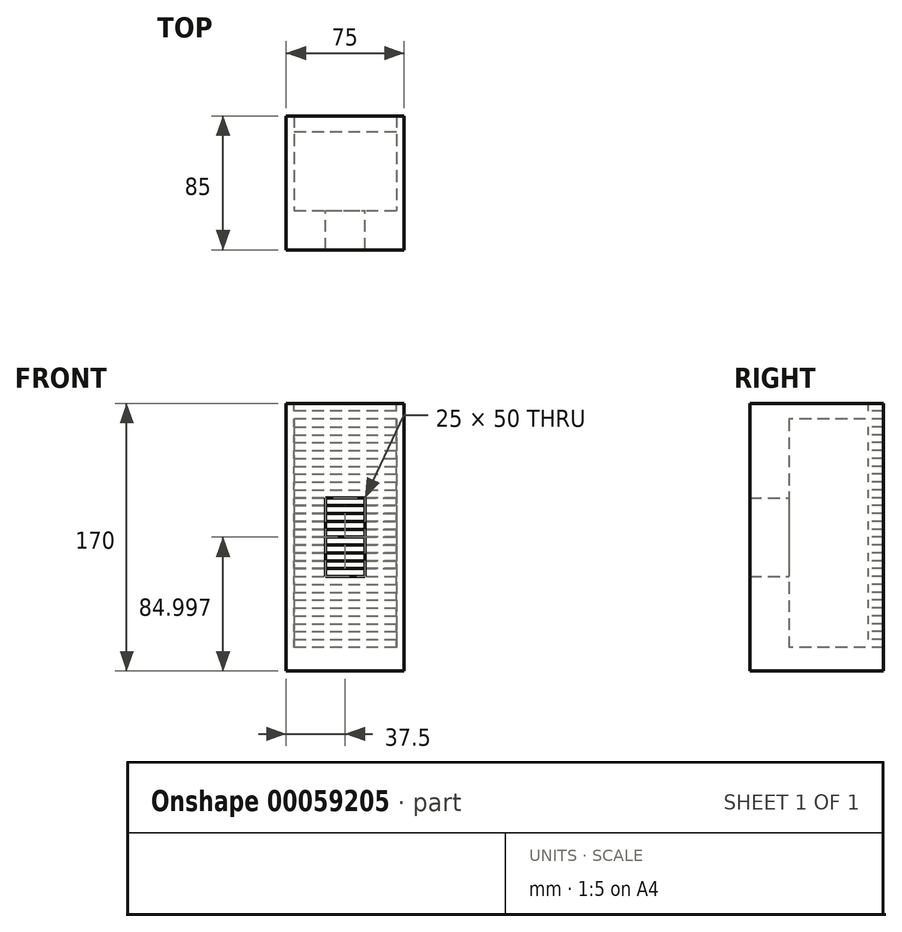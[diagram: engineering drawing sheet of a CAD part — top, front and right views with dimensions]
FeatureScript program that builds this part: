
annotation { "Feature Type Name" : "Feature", "Feature Type Description" : "" }
export const myFeature = defineFeature(function(context is Context, id is Id, definition is map)
    precondition{}
    {
        {
            var Q0;
            Q0=qCreatedBy(makeId("Right.planeOp"),FACE);
            var sketch = newSketch(context, id + "F0", { "sketchPlane" : qUnion([Q0])});
            skLineSegment(sketch, "E0", {"start": v(-41.76, 67.65) * mm, "end": v(-41.76, -102.35) * mm});
            skLineSegment(sketch, "E1", {"start": v(-41.76, -102.35) * mm, "end": v(-31.76, -102.35) * mm});
            skLineSegment(sketch, "E2", {"start": v(-31.76, -102.35) * mm, "end": v(-31.76, 67.65) * mm});
            skLineSegment(sketch, "E3", {"start": v(-31.76, 67.65) * mm, "end": v(-41.76, 67.65) * mm});
            skSolve(sketch);
        }
        {
            var Q0;
            Q0=qSketchRegion(id+"F0",true);
            extrude(context, id + "F1", {"entities" : qUnion([Q0]), "endBound" : BoundingType.SYMMETRIC, "depth" : 75 * mm});
        }
        {
            var Q0;
            Q0=makeQuery(id+"F1.opExtrude","SWEPT_FACE",FACE,{"disambiguationData":[OSD([sQuery(id+"F0.wireOp",EDGE,"E0")])]});
            var sketch = newSketch(context, id + "F2", { "sketchPlane" : qUnion([Q0])});
            skLineSegment(sketch, "E4.bottom", {"start": v(-32.5, 67.55) * mm, "end": v(32.5, 67.55) * mm});
            skLineSegment(sketch, "E4.top", {"start": v(-32.5, 62.65) * mm, "end": v(32.5, 62.65) * mm});
            skLineSegment(sketch, "E4.left", {"start": v(-32.5, 67.55) * mm, "end": v(-32.5, 62.65) * mm});
            skLineSegment(sketch, "E4.right", {"start": v(32.5, 67.55) * mm, "end": v(32.5, 62.65) * mm});
            skLineSegment(sketch, "E5.0.1.0", {"start": v(-32.5, 57.55) * mm, "end": v(32.5, 57.55) * mm});
            skLineSegment(sketch, "E5.0.1.1", {"start": v(-32.5, 57.55) * mm, "end": v(-32.5, 52.65) * mm});
            skLineSegment(sketch, "E5.0.1.2", {"start": v(-32.5, 52.65) * mm, "end": v(32.5, 52.65) * mm});
            skLineSegment(sketch, "E5.0.1.3", {"start": v(32.5, 57.55) * mm, "end": v(32.5, 52.65) * mm});
            skLineSegment(sketch, "E5.0.2.0", {"start": v(-32.5, 47.55) * mm, "end": v(32.5, 47.55) * mm});
            skLineSegment(sketch, "E5.0.2.1", {"start": v(-32.5, 47.55) * mm, "end": v(-32.5, 42.65) * mm});
            skLineSegment(sketch, "E5.0.2.2", {"start": v(-32.5, 42.65) * mm, "end": v(32.5, 42.65) * mm});
            skLineSegment(sketch, "E5.0.2.3", {"start": v(32.5, 47.55) * mm, "end": v(32.5, 42.65) * mm});
            skLineSegment(sketch, "E5.0.3.0", {"start": v(-32.5, 37.55) * mm, "end": v(32.5, 37.55) * mm});
            skLineSegment(sketch, "E5.0.3.1", {"start": v(-32.5, 37.55) * mm, "end": v(-32.5, 32.65) * mm});
            skLineSegment(sketch, "E5.0.3.2", {"start": v(-32.5, 32.65) * mm, "end": v(32.5, 32.65) * mm});
            skLineSegment(sketch, "E5.0.3.3", {"start": v(32.5, 37.55) * mm, "end": v(32.5, 32.65) * mm});
            skLineSegment(sketch, "E5.0.4.0", {"start": v(-32.5, 27.55) * mm, "end": v(32.5, 27.55) * mm});
            skLineSegment(sketch, "E5.0.4.1", {"start": v(-32.5, 27.55) * mm, "end": v(-32.5, 22.65) * mm});
            skLineSegment(sketch, "E5.0.4.2", {"start": v(-32.5, 22.65) * mm, "end": v(32.5, 22.65) * mm});
            skLineSegment(sketch, "E5.0.4.3", {"start": v(32.5, 27.55) * mm, "end": v(32.5, 22.65) * mm});
            skLineSegment(sketch, "E5.direction1", {"start": v(-32.5, 67.55) * mm, "end": v(-7.5, 67.55) * mm, "construction": true});
            skLineSegment(sketch, "E5.direction2", {"start": v(-32.5, 67.55) * mm, "end": v(-32.5, 57.55) * mm, "construction": true});
            skLineSegment(sketch, "E6.0.0.5", {"start": v(-32.5, 17.55) * mm, "end": v(32.5, 17.55) * mm});
            skLineSegment(sketch, "E6.3.0.5", {"start": v(-32.5, 17.55) * mm, "end": v(-32.5, 12.65) * mm});
            skLineSegment(sketch, "E6.6.0.5", {"start": v(-32.5, 12.65) * mm, "end": v(32.5, 12.65) * mm});
            skLineSegment(sketch, "E6.9.0.5", {"start": v(32.5, 17.55) * mm, "end": v(32.5, 12.65) * mm});
            skLineSegment(sketch, "E6.0.0.6", {"start": v(-32.5, 7.55) * mm, "end": v(32.5, 7.55) * mm});
            skLineSegment(sketch, "E6.3.0.6", {"start": v(-32.5, 7.55) * mm, "end": v(-32.5, 2.65) * mm});
            skLineSegment(sketch, "E6.6.0.6", {"start": v(-32.5, 2.65) * mm, "end": v(32.5, 2.65) * mm});
            skLineSegment(sketch, "E6.9.0.6", {"start": v(32.5, 7.55) * mm, "end": v(32.5, 2.65) * mm});
            skLineSegment(sketch, "E6.0.0.7", {"start": v(-32.5, -2.45) * mm, "end": v(32.5, -2.45) * mm});
            skLineSegment(sketch, "E6.3.0.7", {"start": v(-32.5, -2.45) * mm, "end": v(-32.5, -7.35) * mm});
            skLineSegment(sketch, "E6.6.0.7", {"start": v(-32.5, -7.35) * mm, "end": v(32.5, -7.35) * mm});
            skLineSegment(sketch, "E6.9.0.7", {"start": v(32.5, -2.45) * mm, "end": v(32.5, -7.35) * mm});
            skLineSegment(sketch, "E7.0.0.8", {"start": v(-32.5, -12.45) * mm, "end": v(32.5, -12.45) * mm});
            skLineSegment(sketch, "E7.3.0.8", {"start": v(-32.5, -12.45) * mm, "end": v(-32.5, -17.35) * mm});
            skLineSegment(sketch, "E7.6.0.8", {"start": v(-32.5, -17.35) * mm, "end": v(32.5, -17.35) * mm});
            skLineSegment(sketch, "E7.9.0.8", {"start": v(32.5, -12.45) * mm, "end": v(32.5, -17.35) * mm});
            skLineSegment(sketch, "E7.0.0.9", {"start": v(-32.5, -22.45) * mm, "end": v(32.5, -22.45) * mm});
            skLineSegment(sketch, "E7.3.0.9", {"start": v(-32.5, -22.45) * mm, "end": v(-32.5, -27.35) * mm});
            skLineSegment(sketch, "E7.6.0.9", {"start": v(-32.5, -27.35) * mm, "end": v(32.5, -27.35) * mm});
            skLineSegment(sketch, "E7.9.0.9", {"start": v(32.5, -22.45) * mm, "end": v(32.5, -27.35) * mm});
            skLineSegment(sketch, "E7.0.0.10", {"start": v(-32.5, -32.45) * mm, "end": v(32.5, -32.45) * mm});
            skLineSegment(sketch, "E7.3.0.10", {"start": v(-32.5, -32.45) * mm, "end": v(-32.5, -37.35) * mm});
            skLineSegment(sketch, "E7.6.0.10", {"start": v(-32.5, -37.35) * mm, "end": v(32.5, -37.35) * mm});
            skLineSegment(sketch, "E7.9.0.10", {"start": v(32.5, -32.45) * mm, "end": v(32.5, -37.35) * mm});
            skLineSegment(sketch, "E7.0.0.11", {"start": v(-32.5, -42.45) * mm, "end": v(32.5, -42.45) * mm});
            skLineSegment(sketch, "E7.3.0.11", {"start": v(-32.5, -42.45) * mm, "end": v(-32.5, -47.35) * mm});
            skLineSegment(sketch, "E7.6.0.11", {"start": v(-32.5, -47.35) * mm, "end": v(32.5, -47.35) * mm});
            skLineSegment(sketch, "E7.9.0.11", {"start": v(32.5, -42.45) * mm, "end": v(32.5, -47.35) * mm});
            skLineSegment(sketch, "E7.0.0.12", {"start": v(-32.5, -52.45) * mm, "end": v(32.5, -52.45) * mm});
            skLineSegment(sketch, "E7.3.0.12", {"start": v(-32.5, -52.45) * mm, "end": v(-32.5, -57.35) * mm});
            skLineSegment(sketch, "E7.6.0.12", {"start": v(-32.5, -57.35) * mm, "end": v(32.5, -57.35) * mm});
            skLineSegment(sketch, "E7.9.0.12", {"start": v(32.5, -52.45) * mm, "end": v(32.5, -57.35) * mm});
            skLineSegment(sketch, "E7.0.0.13", {"start": v(-32.5, -62.45) * mm, "end": v(32.5, -62.45) * mm});
            skLineSegment(sketch, "E7.3.0.13", {"start": v(-32.5, -62.45) * mm, "end": v(-32.5, -67.35) * mm});
            skLineSegment(sketch, "E7.6.0.13", {"start": v(-32.5, -67.35) * mm, "end": v(32.5, -67.35) * mm});
            skLineSegment(sketch, "E7.9.0.13", {"start": v(32.5, -62.45) * mm, "end": v(32.5, -67.35) * mm});
            skLineSegment(sketch, "E7.0.0.14", {"start": v(-32.5, -72.45) * mm, "end": v(32.5, -72.45) * mm});
            skLineSegment(sketch, "E7.3.0.14", {"start": v(-32.5, -72.45) * mm, "end": v(-32.5, -77.35) * mm});
            skLineSegment(sketch, "E7.6.0.14", {"start": v(-32.5, -77.35) * mm, "end": v(32.5, -77.35) * mm});
            skLineSegment(sketch, "E7.9.0.14", {"start": v(32.5, -72.45) * mm, "end": v(32.5, -77.35) * mm});
            skLineSegment(sketch, "E7.0.0.15", {"start": v(-32.5, -82.45) * mm, "end": v(32.5, -82.45) * mm});
            skLineSegment(sketch, "E7.3.0.15", {"start": v(-32.5, -82.45) * mm, "end": v(-32.5, -87.35) * mm});
            skLineSegment(sketch, "E7.6.0.15", {"start": v(-32.5, -87.35) * mm, "end": v(32.5, -87.35) * mm});
            skLineSegment(sketch, "E7.9.0.15", {"start": v(32.5, -82.45) * mm, "end": v(32.5, -87.35) * mm});
            skSolve(sketch);
        }
        {
            var Q0;
            Q0=qSketchRegion(id+"F2",true);
            extrude(context, id + "F3", {"entities" : qUnion([Q0]), "operationType" : NewBodyOperationType.REMOVE, "endBound" : BoundingType.UP_TO_NEXT, "oppositeDirection" : true, "depth" : 25 * mm});
        }
        {
            var Q0;
            Q0=makeQuery(id+"F1.opExtrude","SWEPT_FACE",FACE,{"disambiguationData":[OSD([sQuery(id+"F0.wireOp",EDGE,"E0")])]});
            var sketch = newSketch(context, id + "F4", { "sketchPlane" : qUnion([Q0])});
            skLineSegment(sketch, "E8", {"start": v(-37.5, 67.65) * mm, "end": v(37.5, 67.65) * mm});
            skLineSegment(sketch, "E9", {"start": v(37.5, 67.65) * mm, "end": v(37.5, -102.35) * mm});
            skLineSegment(sketch, "E10", {"start": v(37.5, -102.35) * mm, "end": v(-37.5, -102.35) * mm});
            skLineSegment(sketch, "E11", {"start": v(-37.5, -102.35) * mm, "end": v(-37.5, 67.65) * mm});
            skLineSegment(sketch, "E12", {"start": v(32.5, 57.55) * mm, "end": v(32.5, -87.35) * mm});
            skLineSegment(sketch, "E13", {"start": v(32.5, -87.35) * mm, "end": v(-32.5, -87.35) * mm});
            skLineSegment(sketch, "E14", {"start": v(-32.5, -87.35) * mm, "end": v(-32.5, 57.55) * mm});
            skLineSegment(sketch, "E15", {"start": v(-32.5, 57.55) * mm, "end": v(32.5, 57.55) * mm});
            skSolve(sketch);
        }
        {
            var Q0;
            Q0 = qSketchRegion(id + "F4", true);
            extrude(context, id + "F5", {"entities" : qUnion([Q0]), "operationType" : NewBodyOperationType.ADD, "depth" : 50 * mm});
        }
        {
            var Q0;
            Q0=makeQuery(id+"F5.opExtrude","CAP_FACE",FACE,{"disambiguationData":[OSD([sQuery(id+"F4.wireOp",EDGE,"E8"),sQuery(id+"F4.wireOp",EDGE,"E9"),sQuery(id+"F4.wireOp",EDGE,"E10"),sQuery(id+"F4.wireOp",EDGE,"E11"),sQuery(id+"F4.wireOp",EDGE,"E12"),sQuery(id+"F4.wireOp",EDGE,"E13"),sQuery(id+"F4.wireOp",EDGE,"E14"),sQuery(id+"F4.wireOp",EDGE,"E15")])],"isStart":false});
            var sketch = newSketch(context, id + "F6", { "sketchPlane" : qUnion([Q0])});
            skLineSegment(sketch, "E16", {"start": v(-37.5, 67.65) * mm, "end": v(37.5, 67.65) * mm});
            skLineSegment(sketch, "E17", {"start": v(37.5, 67.65) * mm, "end": v(37.5, -102.35) * mm});
            skLineSegment(sketch, "E18", {"start": v(37.5, -102.35) * mm, "end": v(-37.5, -102.35) * mm});
            skLineSegment(sketch, "E19", {"start": v(-37.5, -102.35) * mm, "end": v(-37.5, 67.65) * mm});
            skLineSegment(sketch, "E20.bottom", {"start": v(-12.5, 7.65) * mm, "end": v(12.5, 7.65) * mm});
            skLineSegment(sketch, "E20.top", {"start": v(-12.5, -42.35) * mm, "end": v(12.5, -42.35) * mm});
            skLineSegment(sketch, "E20.left", {"start": v(-12.5, 7.65) * mm, "end": v(-12.5, -42.35) * mm});
            skLineSegment(sketch, "E20.right", {"start": v(12.5, 7.65) * mm, "end": v(12.5, -42.35) * mm});
            skLineSegment(sketch, "E21", {"start": v(0, 67.65) * mm, "end": v(0, -102.35) * mm, "construction": true});
            skLineSegment(sketch, "E22", {"start": v(37.5, -17.35) * mm, "end": v(-37.5, -17.35) * mm, "construction": true});
            skSolve(sketch);
        }
        {
            var Q0;
            Q0 = qSketchRegion(id + "F6", true);
            extrude(context, id + "F7", {"entities" : qUnion([Q0]), "operationType" : NewBodyOperationType.ADD, "depth" : 25 * mm});
        }
    });
